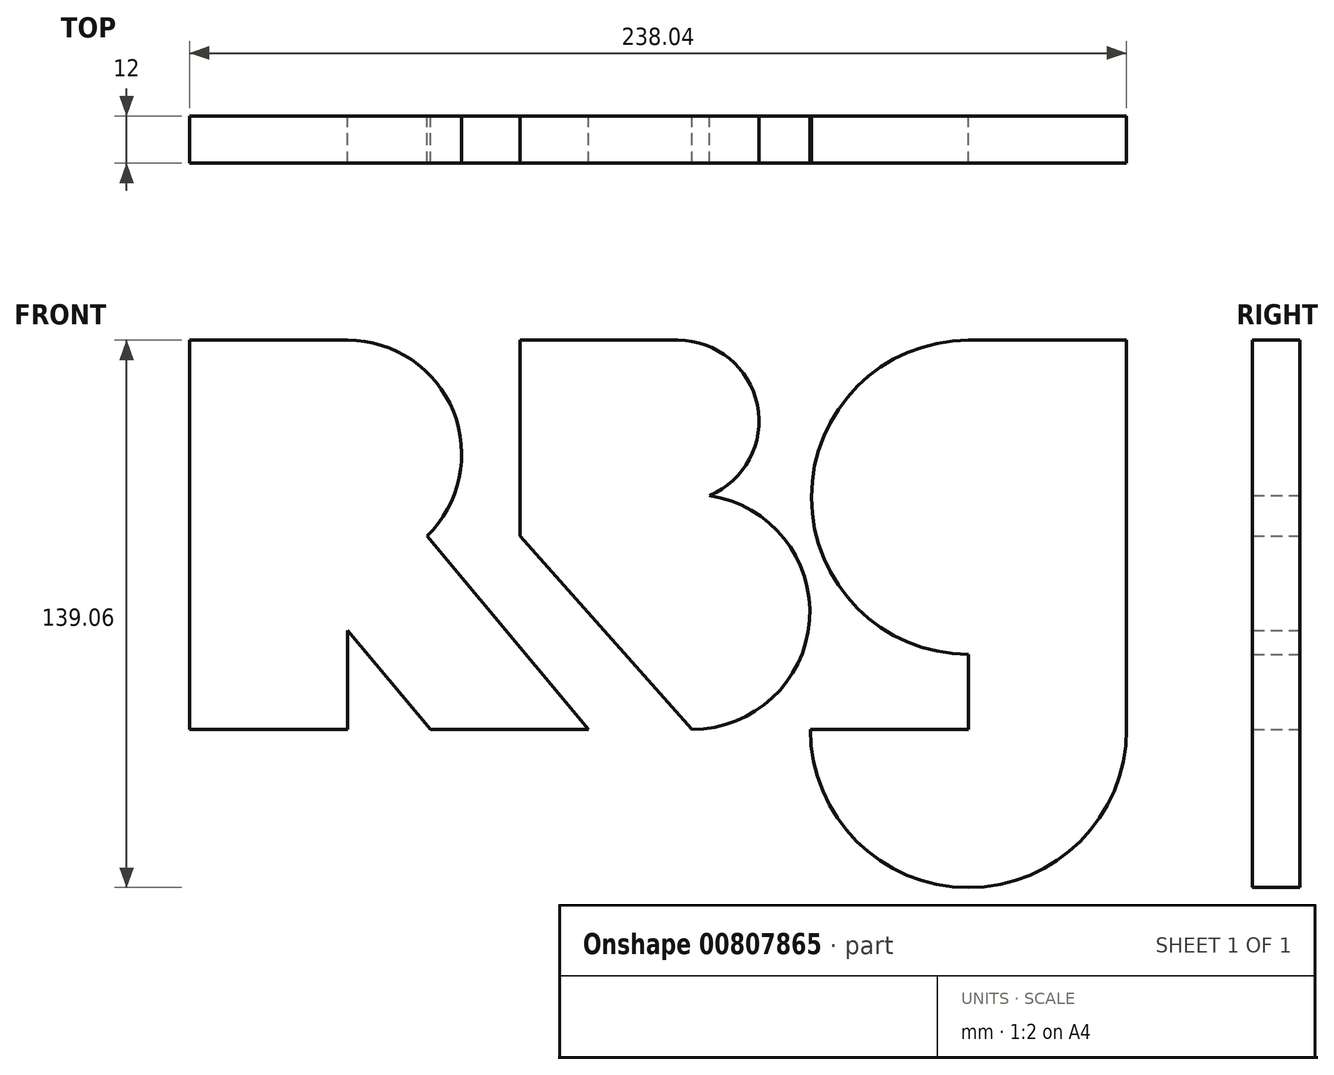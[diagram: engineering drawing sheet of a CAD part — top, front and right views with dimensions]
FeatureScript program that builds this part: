
annotation { "Feature Type Name" : "Feature", "Feature Type Description" : "" }
export const myFeature = defineFeature(function(context is Context, id is Id, definition is map)
    precondition{}
    {
        {
            var Q0;
            Q0=qCreatedBy(makeId("Front.planeOp"),FACE);
            var sketch = newSketch(context, id + "F0", { "sketchPlane" : qUnion([Q0])});
            skLineSegment(sketch, "E0", {"start": v(-60.96, 17.59) * mm, "end": v(-60.96, -15.37) * mm});
            skLineSegment(sketch, "E1", {"start": v(-60.96, -15.37) * mm, "end": v(-47.56, -15.37) * mm});
            skLineSegment(sketch, "E2", {"start": v(-47.56, -15.37) * mm, "end": v(-47.56, -7) * mm});
            skLineSegment(sketch, "E3", {"start": v(-47.56, -7) * mm, "end": v(-40.55, -15.37) * mm});
            skLineSegment(sketch, "E4", {"start": v(-40.55, -15.37) * mm, "end": v(-27.16, -15.37) * mm});
            skLineSegment(sketch, "E5", {"start": v(-27.16, -15.37) * mm, "end": v(-40.87, 1) * mm});
            skLineSegment(sketch, "E6", {"start": v(-60.96, 17.59) * mm, "end": v(-47.56, 17.59) * mm});
            skArc(sketch, "E7", {"start": v(-40.87, 1) * mm, "mid": v(-38.62, 11.55) * mm, "end": v(-47.56, 17.59) * mm});
            skLineSegment(sketch, "E8", {"start": v(-32.98, 1) * mm, "end": v(-32.98, 17.59) * mm});
            skLineSegment(sketch, "E9", {"start": v(-32.98, 17.59) * mm, "end": v(-19.6, 17.59) * mm});
            skArc(sketch, "E10", {"start": v(-16.94, 4.43) * mm, "mid": v(-12.88, 12.1) * mm, "end": v(-19.6, 17.59) * mm});
            skLineSegment(sketch, "E11", {"start": v(5, 17.59) * mm, "end": v(18.39, 17.59) * mm});
            skLineSegment(sketch, "E12", {"start": v(18.39, 17.59) * mm, "end": v(18.39, -15.37) * mm});
            skArc(sketch, "E13", {"start": v(-8.4, -15.37) * mm, "mid": v(5, -28.76) * mm, "end": v(18.39, -15.37) * mm});
            skPoint(sketch, "E13.startSnap0", {"position": v(-54.26, -15.37) * mm});
            skLineSegment(sketch, "E14", {"start": v(-8.4, 17.59) * mm, "end": v(5, 17.59) * mm, "construction": true});
            skLineSegment(sketch, "E15", {"start": v(-8.4, 17.59) * mm, "end": v(-8.4, -36.6) * mm, "construction": true});
            skLineSegment(sketch, "E16", {"start": v(-25.78, -15.37) * mm, "end": v(-18.4, -15.37) * mm, "construction": true});
            skArc(sketch, "E17", {"start": v(-18.4, -15.37) * mm, "mid": v(-8.47, -6.15) * mm, "end": v(-16.94, 4.43) * mm});
            skLineSegment(sketch, "E18", {"start": v(-32.98, 1) * mm, "end": v(-18.4, -15.37) * mm});
            skArc(sketch, "E19", {"start": v(5, 17.59) * mm, "mid": v(-8.3, 4.29) * mm, "end": v(5, -9.01) * mm});
            skLineSegment(sketch, "E20", {"start": v(-8.4, -15.37) * mm, "end": v(5, -15.37) * mm});
            skLineSegment(sketch, "E21", {"start": v(5, -9.01) * mm, "end": v(5, -15.37) * mm});
            skSolve(sketch);
        }
        {
            var Q0;
            Q0 = qSketchRegion(id + "F0", true);
            extrude(context, id + "F1", {"entities" : qUnion([Q0]), "depth" : 4 * mm, "offsetDistance" : 25 * mm});
        }
        {
            var Q0;
            Q0=makeQuery(id+"F1.opExtrude","SWEPT_BODY",BODY,{"disambiguationData":[OSD([sQuery(id+"F0.wireOp",EDGE,"E0"),sQuery(id+"F0.wireOp",EDGE,"E1"),sQuery(id+"F0.wireOp",EDGE,"E2"),sQuery(id+"F0.wireOp",EDGE,"E3"),sQuery(id+"F0.wireOp",EDGE,"E4"),sQuery(id+"F0.wireOp",EDGE,"E5"),sQuery(id+"F0.wireOp",EDGE,"E6"),sQuery(id+"F0.wireOp",EDGE,"E7")])]});
            var Q1;
            Q1=makeQuery(id+"F1.opExtrude","SWEPT_BODY",BODY,{"disambiguationData":[OSD([sQuery(id+"F0.wireOp",EDGE,"E8"),sQuery(id+"F0.wireOp",EDGE,"E9"),sQuery(id+"F0.wireOp",EDGE,"E10"),sQuery(id+"F0.wireOp",EDGE,"E17"),sQuery(id+"F0.wireOp",EDGE,"E18")])]});
            var Q2;
            Q2=makeQuery(id+"F1.opExtrude","SWEPT_BODY",BODY,{"disambiguationData":[OSD([sQuery(id+"F0.wireOp",EDGE,"E11"),sQuery(id+"F0.wireOp",EDGE,"E12"),sQuery(id+"F0.wireOp",EDGE,"E13"),sQuery(id+"F0.wireOp",EDGE,"E19"),sQuery(id+"F0.wireOp",EDGE,"E20"),sQuery(id+"F0.wireOp",EDGE,"E21")])]});
            var Q3;
            Q3=makeQuery(id+"F1.opExtrude","CAP_VERTEX",VERTEX,{"disambiguationData":[OSD([sQuery(id+"F0.wireOp",EDGE,"E0"),sQuery(id+"F0.wireOp",EDGE,"E6")])],"isStart":false});
            transform(context, id + "F2", {"entities" : qUnion([Q0, Q1, Q2]), "transformType" : TransformType.SCALE_UNIFORMLY, "scale" : 3, "scalePoint" : qUnion([Q3]), "makeCopy" : false});
        }
    });
